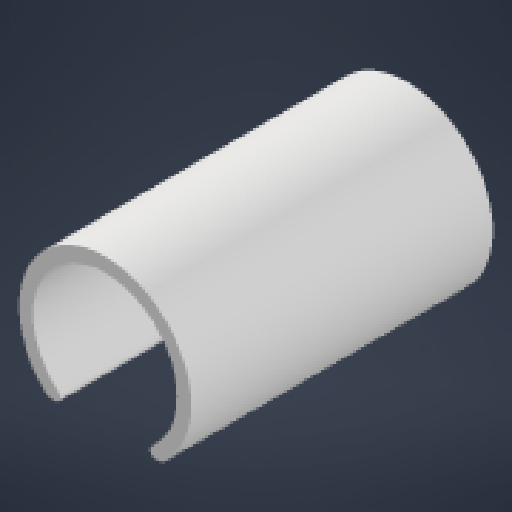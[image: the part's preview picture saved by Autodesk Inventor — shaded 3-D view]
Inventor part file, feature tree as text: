
AUTODESK INVENTOR PART (.ipt)
format: ipt  version: 2024.1 (Build 281209000, 209)  size: 146,944 bytes
history: native  units: in
note: dims shown in document units (in); Inventor stores cm internally (conversion verified against a paired STEP export)
features: other x4, reference x2, extrude x1, fillet x1, sketch x1
ambient origin geometry x8: Origin, YZ Plane, XZ Plane, XY Plane, X Axis, Y Axis, Z Axis, Center Point
bodies: Solid1 (feature_tree)
feature tree (9):
  extrude  "Extrusion1"  Depth=0.005in
  fillet  "Fillet1"  Radius=0.273in
  sketch  "Sketch1"  dims[d0=0.002in d1=0.005in d2=0.273in d3=0.0in d4=0.005in]
  reference  "Reference1"
  reference  "Reference2"
  other  "<userpath>\Documents\School\FallCAD\Bio\Bio.iam"
  other  "Bio.iam"
  other  "Servo HS425BB:1"
  other  "ServoMount:1"
